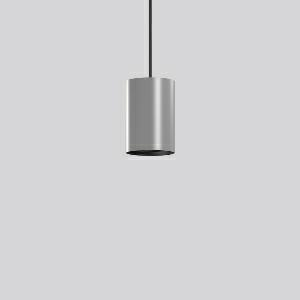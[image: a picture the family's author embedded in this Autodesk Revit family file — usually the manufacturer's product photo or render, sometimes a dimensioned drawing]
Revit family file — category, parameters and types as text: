
# Revit family: deecos_p_maxi_911539_004_3_75ee
name_source: partatom
category: Lighting Fixtures
units: mm (PartAtom-declared; Revit-internal decimal feet)

## family parameters
Cut with Voids When Loaded = No
Host = Face
Light Source = No
Part Type = Normal
Room Calculation Point = No
Round Connector Dimension = Use Diameter
Shared = No

## types (1)
- DEECOS P maxi (1 x LED Modul 935, 4200 lm, 3500)
    Apparent Load = 35 VA
    Approval mark = CE
    CIE Flux Codes = 97 100 100 100 100
    Color Rendering = 92
    Color Temperature = 3500
    Default Elevation = 1800 mm
    Description = Series: DEECOS P maxi
Cylindrical pendant luminaire. Housing: die-cast aluminium, powder-coated. Canopy made of powder-coated sheet steel with magnetic attachment. Optical assembly with reflector made of MIRO-Silver with 98% total light reflection for outstanding efficiency - can be changed without tools. Best colour rendering index Ra>90. Transparent suspension cable 2 m, can be shortened. High quality converter without flickering and stroboscopic effect. The following accessories can be mounted without use of tools: interchangeable lenses, honeycomb louvre, clear and frosted diffusers, white interchangeable plastic ring. Decorative recessed suspension set available as accessory. 
Colour: silver
Diameter: 123 mm
Height: 181 mm
Suspension length: 2000 mm
Lamp: LED
Socket: without socket
Colour temperature: 3500K
Colour rendering index (CRI): 92
System power: 35 W
Rated luminous flux: 4200 lm
Luminous efficiency: 120 lm/W
Control gear: Regulated power supply
Protection class: I
Type of protection: IP 20
    Height = 181 mm
    Lamp = 1 x LED Modul 935
    Lamp Light Flux = 4200 lm
    Lamp count = 1
    Length = 123 mm
    Lifetime = 50000 h
    Luminous efficacy = 120 lm/W
    Manufacturer = RZB
    ModVariant = No
    Model = 911539.004.3
    Mounting Place = Ceiling
    Mounting Type = Pendant
    Number of Poles = 1
    OnlyDefault = Yes
    Power Factor = 1
    Product Name = DEECOS P maxi
    Product group = Pendant luminaires
    ProductGroupID = 902
    Protection Class = Protection class I
    Protection Degree = IP 20
    RLX_Detail_Level = 1
    RLX_Emergency_Light_Flux = 0 lm
    RLX_Emergency_Type = 0
    RLX_Emergency_Type_DB = No
    RlxData = <blob elided: 35797 chars, md5=34b2a00f>
    Socket = socket
    Standby Power = 0 W
    System Light Flux = 4200 lm
    System Power = 35 W
    Type Comments = Product without accessories
    Type Image = 911480.004.jpg
    URL = http://relux.com
    VarID = ---
    Voltage = 230 V
    Voltage Range = 220-240 V
    Weight = 0.00 kg
    Width = 0 mm  [stored 0 ft]

note: [stored X ft] marks values corroborated as IEEE doubles in the binary element streams (Revit-internal decimal feet)

## geometry (parser evidence)
native form markers: Blend x4, Sweep x10
no freeform markers — native parametric forms only
